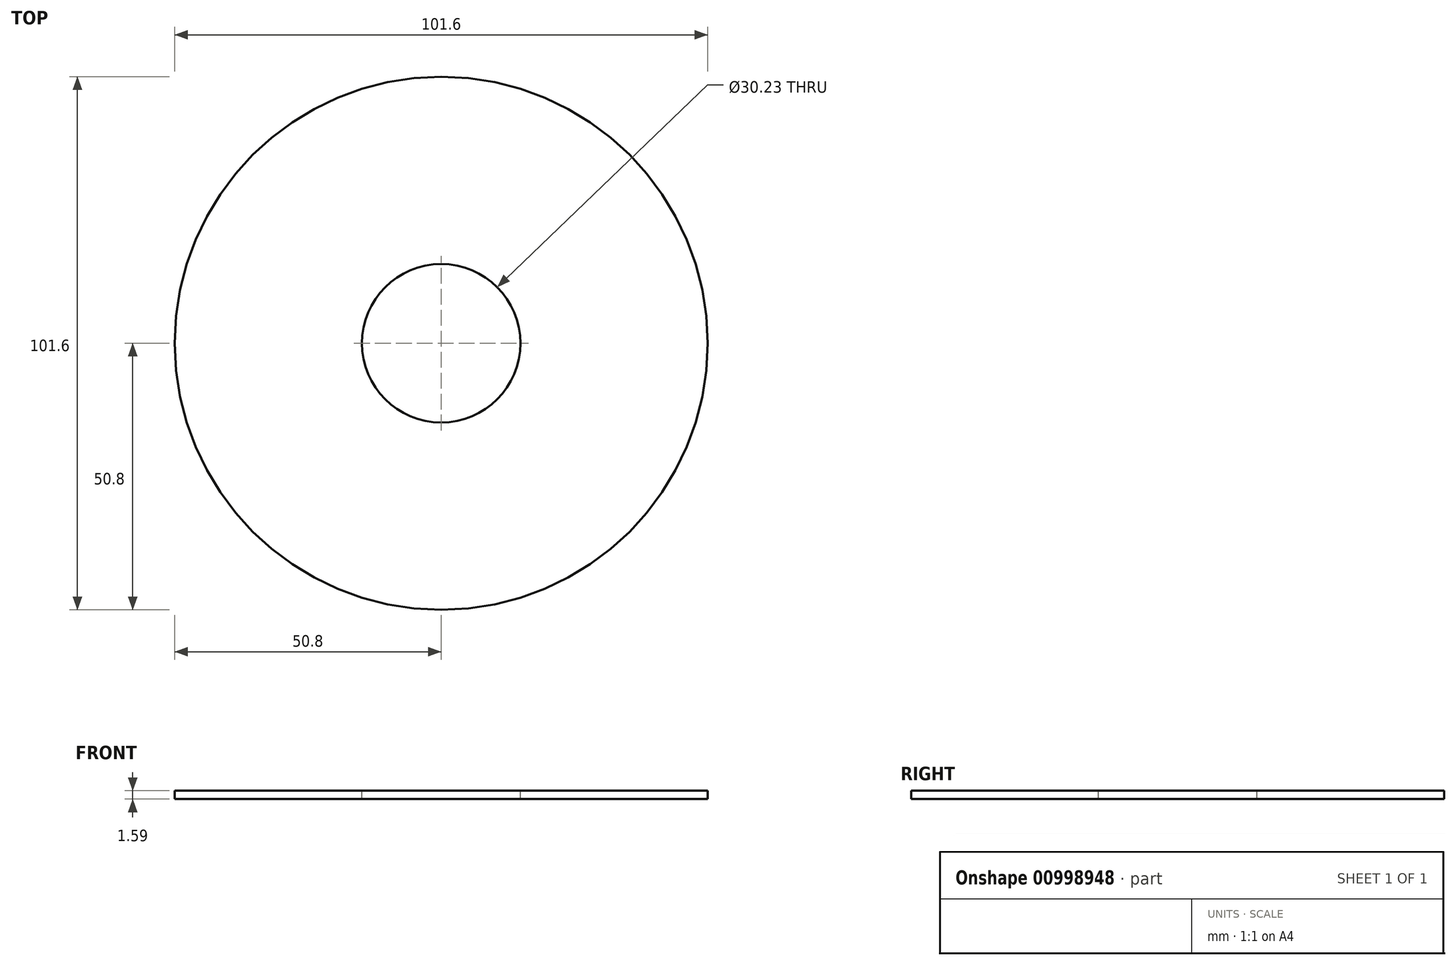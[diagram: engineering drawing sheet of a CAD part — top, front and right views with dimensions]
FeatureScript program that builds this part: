
annotation { "Feature Type Name" : "Feature", "Feature Type Description" : "" }
export const myFeature = defineFeature(function(context is Context, id is Id, definition is map)
    precondition{}
    {
        {
            var Q0;
            Q0=qCreatedBy(makeId("Top.planeOp"),FACE);
            var sketch = newSketch(context, id + "F0", { "sketchPlane" : qUnion([Q0])});
            skCircle(sketch, "E0", {"center": v(0, 0) * mm, "radius": 50.8 * mm});
            skSolve(sketch);
        }
        {
            var Q0;
            Q0=makeQuery(id+"F0.imprint","IMPRINT",FACE,{"disambiguationData":[TD([[makeQuery(id+"F0.imprint","IMPRINT",EDGE,{"derivedFrom":sQuery(id+"F0.wireOp",EDGE,"E0")}),1.0]])]});
            extrude(context, id + "F1", {"entities" : qUnion([Q0]), "depth" : 1.59 * mm, "offsetDistance" : 25.4 * mm});
        }
        {
            var Q0;
            Q0=qCreatedBy(makeId("Top.planeOp"),FACE);
            var sketch = newSketch(context, id + "F2", { "sketchPlane" : qUnion([Q0])});
            skCircle(sketch, "E1", {"center": v(0, 0) * mm, "radius": 15.11 * mm});
            skSolve(sketch);
        }
        {
            var Q0;
            Q0=sQuery(id+"F2.wireOp",VERTEX,"E1.center");
            var Q1;
            Q1=makeQuery(id+"F1.opExtrude","SWEPT_BODY",BODY,{"disambiguationData":[OSD([sQuery(id+"F0.wireOp",EDGE,"E0")])]});
            hole(context, id + "F3", {"style" : HoleStyle.SIMPLE, "endStyle" : HoleEndStyle.BLIND, "oppositeDirection" : true, "holeDiameter" : 30.23 * mm, "majorDiameter" : 6.35 * mm, "holeDepth" : 3.17 * mm, "isTappedThrough" : true, "tappedDepth" : 12.7 * mm, "tapClearance" : 3, "locations" : qUnion([Q0]), "scope" : qUnion([Q1]), "startStyle" : HoleStartStyle.PART});
        }
    });
